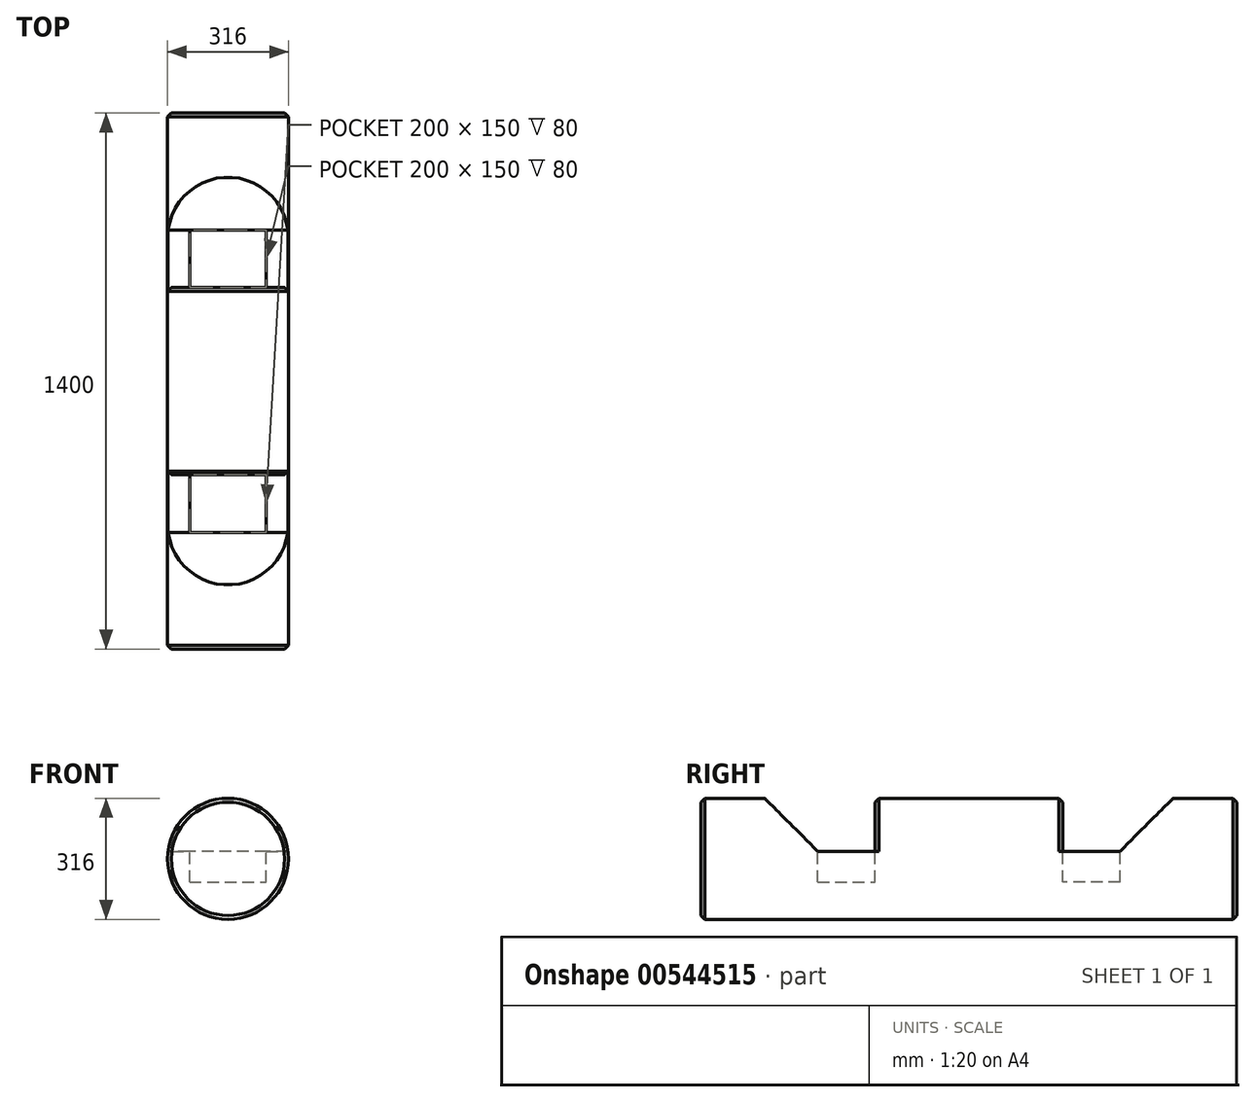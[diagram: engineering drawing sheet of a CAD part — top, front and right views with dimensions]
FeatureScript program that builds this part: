
annotation { "Feature Type Name" : "Feature", "Feature Type Description" : "" }
export const myFeature = defineFeature(function(context is Context, id is Id, definition is map)
    precondition{}
    {
        {
            var Q0;
            Q0=qCreatedBy(makeId("Front.planeOp"),FACE);
            var sketch = newSketch(context, id + "F0", { "sketchPlane" : qUnion([Q0])});
            skCircle(sketch, "E0", {"center": v(0, 0) * mm, "radius": 158 * mm});
            skSolve(sketch);
        }
        {
            var Q0;
            Q0=makeQuery(id+"F0.imprint","IMPRINT",FACE,{"disambiguationData":[TD([[makeQuery(id+"F0.imprint","IMPRINT",EDGE,{"derivedFrom":sQuery(id+"F0.wireOp",EDGE,"E0")}),1.0]])]});
            extrude(context, id + "F1", {"entities" : qUnion([Q0]), "oppositeDirection" : true, "depth" : 1400 * mm, "offsetDistance" : 25 * mm});
        }
        {
            var Q0;
            Q0=qCreatedBy(makeId("Right.planeOp"),FACE);
            var sketch = newSketch(context, id + "F2", { "sketchPlane" : qUnion([Q0])});
            skLineSegment(sketch, "E1", {"start": v(0, 0) * mm, "end": v(1400, 0) * mm, "construction": true});
            skLineSegment(sketch, "E2", {"start": v(700, 0) * mm, "end": v(390, 0) * mm, "construction": true});
            skLineSegment(sketch, "E3", {"start": v(390, 0) * mm, "end": v(390, 20) * mm, "construction": true});
            skLineSegment(sketch, "E4", {"start": v(390, 20) * mm, "end": v(167, 20) * mm});
            skLineSegment(sketch, "E5", {"start": v(167, 20) * mm, "end": v(167, 158) * mm});
            skLineSegment(sketch, "E6", {"start": v(167, 158) * mm, "end": v(455, 158) * mm});
            skLineSegment(sketch, "E7", {"start": v(455, 158) * mm, "end": v(455, 20) * mm});
            skLineSegment(sketch, "E8", {"start": v(455, 20) * mm, "end": v(390, 20) * mm});
            skLineSegment(sketch, "E9", {"start": v(700, 0) * mm, "end": v(700, 69.97) * mm, "construction": true});
            skLineSegment(sketch, "E10.MirrorCS", {"start": v(945, 20) * mm, "end": v(1010, 20) * mm});
            skLineSegment(sketch, "E11.MirrorCS", {"start": v(945, 158) * mm, "end": v(945, 20) * mm});
            skLineSegment(sketch, "E12.MirrorCS", {"start": v(1233, 158) * mm, "end": v(945, 158) * mm});
            skLineSegment(sketch, "E13.MirrorCS", {"start": v(1233, 20) * mm, "end": v(1233, 158) * mm});
            skLineSegment(sketch, "E14.MirrorCS", {"start": v(1010, 0) * mm, "end": v(1010, 20) * mm, "construction": true});
            skLineSegment(sketch, "E15.MirrorCS", {"start": v(1010, 20) * mm, "end": v(1233, 20) * mm});
            skLineSegment(sketch, "E16.MirrorCS", {"start": v(700, 0) * mm, "end": v(1010, 0) * mm, "construction": true});
            skSolve(sketch);
        }
        {
            var Q0;
            Q0=makeQuery(id+"F2.imprint","IMPRINT",FACE,{"disambiguationData":[TD([[makeQuery(id+"F2.imprint","IMPRINT",EDGE,{"derivedFrom":sQuery(id+"F2.wireOp",EDGE,"E4")}),-1.0]])]});
            var Q1;
            Q1=makeQuery(id+"F2.imprint","IMPRINT",FACE,{"disambiguationData":[TD([[makeQuery(id+"F2.imprint","IMPRINT",EDGE,{"derivedFrom":sQuery(id+"F2.wireOp",EDGE,"E10.MirrorCS")}),1.0]])]});
            extrude(context, id + "F3", {"entities" : qUnion([Q0, Q1]), "operationType" : NewBodyOperationType.REMOVE, "endBound" : BoundingType.THROUGH_ALL, "oppositeDirection" : true, "depth" : 25 * mm, "offsetDistance" : 25 * mm});
        }
        {
            var Q0;
            Q0=makeQuery(id+"F3.boolean.opBoolean","COPY",FACE,{"derivedFrom":makeQuery(id+"F3.opExtrude","CAP_FACE",FACE,{"disambiguationData":[OSD([sQuery(id+"F2.wireOp",EDGE,"E10.MirrorCS"),sQuery(id+"F2.wireOp",EDGE,"E11.MirrorCS"),sQuery(id+"F2.wireOp",EDGE,"E12.MirrorCS"),sQuery(id+"F2.wireOp",EDGE,"E13.MirrorCS"),sQuery(id+"F2.wireOp",EDGE,"E15.MirrorCS")])],"isStart":true})});
            var Q1;
            Q1=makeQuery(id+"F3.boolean.opBoolean","COPY",FACE,{"derivedFrom":makeQuery(id+"F3.opExtrude","CAP_FACE",FACE,{"disambiguationData":[OSD([sQuery(id+"F2.wireOp",EDGE,"E4"),sQuery(id+"F2.wireOp",EDGE,"E5"),sQuery(id+"F2.wireOp",EDGE,"E6"),sQuery(id+"F2.wireOp",EDGE,"E7"),sQuery(id+"F2.wireOp",EDGE,"E8")])],"isStart":true})});
            extrude(context, id + "F4", {"entities" : qUnion([Q0, Q1]), "operationType" : NewBodyOperationType.REMOVE, "endBound" : BoundingType.THROUGH_ALL, "oppositeDirection" : true, "depth" : 25 * mm, "offsetDistance" : 25 * mm});
        }
        {
            var Q0;
            {var subQ0=sQuery(id+"F2.wireOp",EDGE,"E15.MirrorCS");var subQ1=sQuery(id+"F2.wireOp",EDGE,"E13.MirrorCS");Q0=makeQuery(id+"F4.boolean.opBoolean","MERGE",EDGE,{"derivedFrom":[makeQuery(id+"F3.boolean.opBoolean","COPY",EDGE,{"derivedFrom":makeQuery(id+"F3.opExtrude","SWEPT_EDGE",EDGE,{"disambiguationData":[OSD([subQ1,subQ0])]})}),makeQuery(id+"F4.opExtrude","SWEPT_EDGE",EDGE,{"disambiguationData":[OSD([subQ1,subQ0])]})]});}
            chamfer(context, id + "F5", {"entities" : qUnion([Q0]), "width" : 138 * mm, "tangentPropagation" : true});
        }
        {
            var Q0;
            {var subQ0=sQuery(id+"F2.wireOp",EDGE,"E5");var subQ1=sQuery(id+"F2.wireOp",EDGE,"E4");Q0=makeQuery(id+"F4.boolean.opBoolean","MERGE",EDGE,{"derivedFrom":[makeQuery(id+"F3.boolean.opBoolean","COPY",EDGE,{"derivedFrom":makeQuery(id+"F3.opExtrude","SWEPT_EDGE",EDGE,{"disambiguationData":[OSD([subQ1,subQ0])]})}),makeQuery(id+"F4.opExtrude","SWEPT_EDGE",EDGE,{"disambiguationData":[OSD([subQ1,subQ0])]})]});}
            chamfer(context, id + "F6", {"entities" : qUnion([Q0]), "width" : 138 * mm, "tangentPropagation" : true});
        }
        {
            var Q0;
            {var subQ0=sQuery(id+"F2.wireOp",EDGE,"E15.MirrorCS");var subQ1=sQuery(id+"F2.wireOp",EDGE,"E10.MirrorCS");Q0=makeQuery(id+"F4.boolean.opBoolean","MERGE",FACE,{"derivedFrom":[makeQuery(id+"F3.boolean.opBoolean","COPY",FACE,{"derivedFrom":makeQuery(id+"F3.opExtrude","SWEPT_FACE",FACE,{"disambiguationData":[OSD([subQ1,subQ0])]})}),makeQuery(id+"F4.opExtrude","SWEPT_FACE",FACE,{"disambiguationData":[OSD([subQ1,subQ0])]})]});}
            var sketch = newSketch(context, id + "F7", { "sketchPlane" : qUnion([Q0])});
            skLineSegment(sketch, "E17", {"start": v(0, 1095) * mm, "end": v(100, 1095) * mm});
            skLineSegment(sketch, "E18", {"start": v(100, 1095) * mm, "end": v(100, 945) * mm});
            skLineSegment(sketch, "E19", {"start": v(100, 945) * mm, "end": v(-100, 945) * mm});
            skLineSegment(sketch, "E20", {"start": v(-100, 945) * mm, "end": v(-100, 1095) * mm});
            skLineSegment(sketch, "E21", {"start": v(-100, 1095) * mm, "end": v(0, 1095) * mm});
            skSolve(sketch);
        }
        {
            var Q0;
            {var subQ0=sQuery(id+"F2.wireOp",EDGE,"E8");var subQ1=sQuery(id+"F2.wireOp",EDGE,"E4");Q0=makeQuery(id+"F4.boolean.opBoolean","MERGE",FACE,{"derivedFrom":[makeQuery(id+"F3.boolean.opBoolean","COPY",FACE,{"derivedFrom":makeQuery(id+"F3.opExtrude","SWEPT_FACE",FACE,{"disambiguationData":[OSD([subQ1,subQ0])]})}),makeQuery(id+"F4.opExtrude","SWEPT_FACE",FACE,{"disambiguationData":[OSD([subQ1,subQ0])]})]});}
            var sketch = newSketch(context, id + "F8", { "sketchPlane" : qUnion([Q0])});
            skLineSegment(sketch, "E22", {"start": v(0, 305) * mm, "end": v(100, 305) * mm});
            skLineSegment(sketch, "E23", {"start": v(100, 305) * mm, "end": v(100, 455) * mm});
            skLineSegment(sketch, "E24", {"start": v(100, 455) * mm, "end": v(-100, 455) * mm});
            skLineSegment(sketch, "E25", {"start": v(-100, 455) * mm, "end": v(-100, 305) * mm});
            skLineSegment(sketch, "E26", {"start": v(-100, 305) * mm, "end": v(0, 305) * mm});
            skSolve(sketch);
        }
        {
            var Q0;
            Q0=makeQuery(id+"F7.imprint","IMPRINT",FACE,{"disambiguationData":[TD([[makeQuery(id+"F7.imprint","IMPRINT",EDGE,{"derivedFrom":sQuery(id+"F7.wireOp",EDGE,"E17")}),1.0]])]});
            var Q1;
            Q1=makeQuery(id+"F8.imprint","IMPRINT",FACE,{"disambiguationData":[TD([[makeQuery(id+"F8.imprint","IMPRINT",EDGE,{"derivedFrom":sQuery(id+"F8.wireOp",EDGE,"E22")}),1.0]])]});
            extrude(context, id + "F9", {"entities" : qUnion([Q0, Q1]), "operationType" : NewBodyOperationType.REMOVE, "oppositeDirection" : true, "depth" : 80 * mm, "offsetDistance" : 25 * mm});
        }
        {
            var Q0;
            Q0=makeQuery(id+"F1.opExtrude","CAP_EDGE",EDGE,{"disambiguationData":[OSD([sQuery(id+"F0.wireOp",EDGE,"E0")])],"isStart":true});
            var Q1;
            Q1=makeQuery(id+"F1.opExtrude","CAP_EDGE",EDGE,{"disambiguationData":[OSD([sQuery(id+"F0.wireOp",EDGE,"E0")])],"isStart":false});
            chamfer(context, id + "F10", {"entities" : qUnion([Q0, Q1]), "width" : 10 * mm, "tangentPropagation" : true});
        }
        {
            var Q0;
            Q0=makeQuery(id+"F4.boolean.opBoolean","INTERSECT",EDGE,{"derivedFrom":[makeQuery(id+"F1.opExtrude","SWEPT_FACE",FACE,{"disambiguationData":[OSD([sQuery(id+"F0.wireOp",EDGE,"E0")])]}),makeQuery(id+"F4.opExtrude","SWEPT_FACE",FACE,{"disambiguationData":[OSD([sQuery(id+"F2.wireOp",EDGE,"E7")])]})]});
            var Q1;
            Q1=makeQuery(id+"F4.boolean.opBoolean","INTERSECT",EDGE,{"derivedFrom":[makeQuery(id+"F1.opExtrude","SWEPT_FACE",FACE,{"disambiguationData":[OSD([sQuery(id+"F0.wireOp",EDGE,"E0")])]}),makeQuery(id+"F4.opExtrude","SWEPT_FACE",FACE,{"disambiguationData":[OSD([sQuery(id+"F2.wireOp",EDGE,"E11.MirrorCS")])]})]});
            chamfer(context, id + "F11", {"entities" : qUnion([Q0, Q1]), "width" : 10 * mm, "tangentPropagation" : true});
        }
    });
